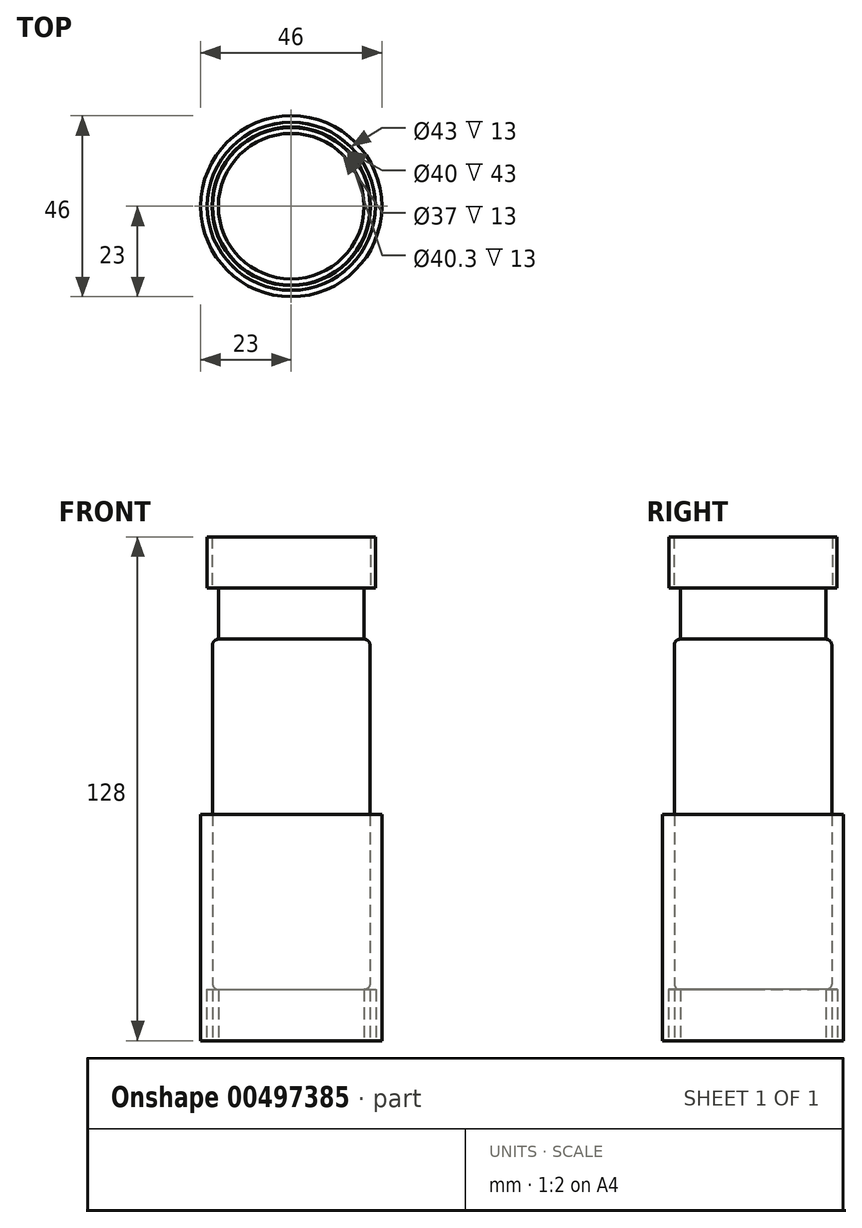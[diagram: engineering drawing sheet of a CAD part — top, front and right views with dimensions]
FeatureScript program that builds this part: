
annotation { "Feature Type Name" : "Feature", "Feature Type Description" : "" }
export const myFeature = defineFeature(function(context is Context, id is Id, definition is map)
    precondition{}
    {
        {
            var Q0;
            Q0=qCreatedBy(makeId("Front.planeOp"),FACE);
            var sketch = newSketch(context, id + "F0", { "sketchPlane" : qUnion([Q0])});
            skLineSegment(sketch, "E0", {"start": v(0, 0) * mm, "end": v(23, 0) * mm});
            skLineSegment(sketch, "E1.bottom", {"start": v(23, 0) * mm, "end": v(21.5, 0) * mm});
            skLineSegment(sketch, "E1.top", {"start": v(23, -13) * mm, "end": v(21.5, -13) * mm});
            skLineSegment(sketch, "E1.left", {"start": v(23, 0) * mm, "end": v(23, -13) * mm});
            skLineSegment(sketch, "E1.right", {"start": v(21.5, 0) * mm, "end": v(21.5, -13) * mm});
            skLineSegment(sketch, "E2.bottom", {"start": v(21.5, -13) * mm, "end": v(20, -13) * mm});
            skLineSegment(sketch, "E2.top", {"start": v(21.5, 0) * mm, "end": v(20, 0) * mm});
            skLineSegment(sketch, "E2.left", {"start": v(21.5, -13) * mm, "end": v(21.5, 0) * mm});
            skLineSegment(sketch, "E2.right", {"start": v(20, -13) * mm, "end": v(20, 0) * mm});
            skLineSegment(sketch, "E3.bottom", {"start": v(20, -13) * mm, "end": v(18.5, -13) * mm});
            skLineSegment(sketch, "E3.top", {"start": v(20, 0) * mm, "end": v(18.5, 0) * mm});
            skLineSegment(sketch, "E3.right", {"start": v(18.5, -13) * mm, "end": v(18.5, 0) * mm});
            skLineSegment(sketch, "E4.bottom", {"start": v(23, 0) * mm, "end": v(0, 0) * mm});
            skLineSegment(sketch, "E4.top", {"start": v(23, 102) * mm, "end": v(0, 102) * mm});
            skLineSegment(sketch, "E4.left", {"start": v(23, 0) * mm, "end": v(23, 102) * mm});
            skLineSegment(sketch, "E4.right", {"start": v(0, 0) * mm, "end": v(0, 102) * mm});
            skLineSegment(sketch, "E5.bottom", {"start": v(21.35, 102) * mm, "end": v(20.15, 102) * mm});
            skLineSegment(sketch, "E5.top", {"start": v(21.35, 115) * mm, "end": v(20.15, 115) * mm});
            skLineSegment(sketch, "E5.left", {"start": v(21.35, 102) * mm, "end": v(21.35, 115) * mm});
            skLineSegment(sketch, "E5.right", {"start": v(20.15, 102) * mm, "end": v(20.15, 115) * mm});
            skLineSegment(sketch, "E6", {"start": v(0, 44.5) * mm, "end": v(23, 44.5) * mm});
            skLineSegment(sketch, "E7.bottom", {"start": v(20, 0) * mm, "end": v(23, 0) * mm});
            skLineSegment(sketch, "E7.top", {"start": v(20, 44.5) * mm, "end": v(23, 44.5) * mm});
            skLineSegment(sketch, "E7.left", {"start": v(20, 0) * mm, "end": v(20, 44.5) * mm});
            skLineSegment(sketch, "E7.right", {"start": v(23, 0) * mm, "end": v(23, 44.5) * mm});
            skLineSegment(sketch, "E8.bottom", {"start": v(18.5, 0) * mm, "end": v(20, 0) * mm});
            skLineSegment(sketch, "E8.top", {"start": v(18.5, 1.5) * mm, "end": v(20, 1.5) * mm});
            skLineSegment(sketch, "E8.left", {"start": v(18.5, 0) * mm, "end": v(18.5, 1.5) * mm});
            skLineSegment(sketch, "E8.right", {"start": v(20, 0) * mm, "end": v(20, 1.5) * mm});
            skArc(sketch, "E9", {"start": v(18.5, 0) * mm, "mid": v(19.56, 0.44) * mm, "end": v(20, 1.5) * mm});
            skLineSegment(sketch, "E10.MirrorCS", {"start": v(20, 89) * mm, "end": v(20, 44.5) * mm});
            skArc(sketch, "E11.MirrorCS", {"start": v(18.5, 89) * mm, "mid": v(19.56, 88.56) * mm, "end": v(20, 87.5) * mm});
            skLineSegment(sketch, "E12", {"start": v(18.5, 89) * mm, "end": v(18.5, 102) * mm});
            skSolve(sketch);
        }
        {
            var Q0;
            {var subQ10=sQuery(id+"F0.wireOp",EDGE,"E11.MirrorCS");Q0=makeQuery(id+"F0.imprint","IMPRINT",FACE,{"disambiguationData":[TD([[makeQuery(id+"F0.imprint","IMPRINT",EDGE,{"derivedFrom":subQ10}),1.0]])]});}
            var Q1;
            {var subQ5=sQuery(id+"F0.wireOp",EDGE,"E0");var subQ6=makeQuery(id+"F0.imprint","INTERSECT",VERTEX,{"derivedFrom":[subQ5,sQuery(id+"F0.wireOp",EDGE,"E1.right")]});Q1=makeQuery(id+"F0.imprint","IMPRINT",FACE,{"disambiguationData":[TD([[makeQuery(id+"F0.imprint","IMPRINT",EDGE,{"disambiguationData":[TD([[subQ6,-1.0]])],"derivedFrom":subQ5}),1.0]])]});}
            var Q2;
            Q2=makeQuery(id+"F0.imprint","IMPRINT",FACE,{"disambiguationData":[TD([[makeQuery(id+"F0.imprint","IMPRINT",EDGE,{"derivedFrom":sQuery(id+"F0.wireOp",EDGE,"E1.top")}),-1.0]])]});
            var Q3;
            {var subQ0=sQuery(id+"F0.wireOp",EDGE,"E2.right");Q3=makeQuery(id+"F0.imprint","IMPRINT",FACE,{"disambiguationData":[TD([[makeQuery(id+"F0.imprint","IMPRINT",EDGE,{"derivedFrom":subQ0}),1.0]])]});}
            var Q4;
            {var subQ3=sQuery(id+"F0.wireOp",EDGE,"E9");Q4=makeQuery(id+"F0.imprint","IMPRINT",FACE,{"disambiguationData":[TD([[makeQuery(id+"F0.imprint","IMPRINT",EDGE,{"derivedFrom":subQ3}),-1.0]])]});}
            var Q5;
            Q5=makeQuery(id+"F0.imprint","IMPRINT",FACE,{"disambiguationData":[TD([[makeQuery(id+"F0.imprint","IMPRINT",EDGE,{"derivedFrom":sQuery(id+"F0.wireOp",EDGE,"E5.top")}),1.0]])]});
            var Q6;
            Q6=sQuery(id+"F0.wireOp",EDGE,"E4.right");
            revolve(context, id + "F1", {"entities" : qUnion([Q0, Q1, Q2, Q3, Q4, Q5]), "axis" : qUnion([Q6]), "revolveType" : RevolveType.FULL});
        }
    });
